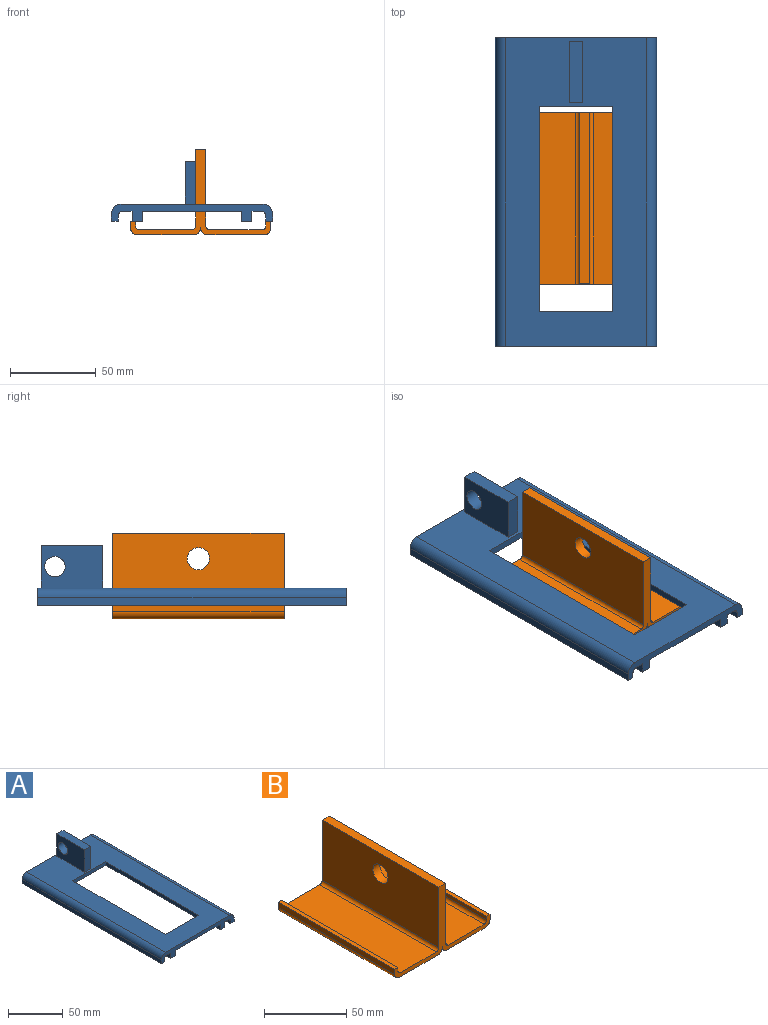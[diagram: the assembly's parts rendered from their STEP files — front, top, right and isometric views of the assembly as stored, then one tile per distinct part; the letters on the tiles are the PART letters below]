
ASSEMBLY  parts=2 mates=1
PART A: 32 faces, bbox 94x180x35 mm
  f0: plane 180x58mm, normal (0,0,-1), area 5304mm2, adj f5,f6,f20,f21,f22,f23,f24,f25
  f1: plane 180x82.8mm, normal (0,0,1), area 9480mm2, adj f14,f15,f20,f21,f22,f23,f24,f25
  f2: plane 180x5.2mm, normal (0,0,-1), area 936mm2, adj f3,f19,f20,f21
  f3: plane 180x6mm, normal (-1,0,0), area 1080mm2, adj f2,f4,f20,f21
  f4: plane 180x6mm, normal (0,0,-1), area 1080mm2, adj f3,f5,f20,f21
  f5: plane 180x6mm, normal (1,0,0), area 1080mm2, adj f0,f4,f20,f21
  f6: plane 180x6mm, normal (-1,0,0), area 1080mm2, adj f0,f7,f20,f21
  f7: plane 180x6mm, normal (0,0,-1), area 1080mm2, adj f6,f8,f20,f21
  f8: plane 180x6mm, normal (1,0,0), area 1080mm2, adj f7,f9,f20,f21
  f9: plane 180x5.2mm, normal (0,0,-1), area 936mm2, adj f8,f10,f20,f21
  f10: cylinder r=2.8mm len=180mm, axis (0,1,0), area 791.7mm2, adj f9,f11,f20,f21
  f11: plane 180x3.2mm, normal (-1,0,0), area 576mm2, adj f10,f12,f20,f21
  f12: plane 180x4mm, normal (0,0,-1), area 720mm2, adj f11,f13,f20,f21
  f13: plane 180x4.4mm, normal (1,0,0), area 792mm2, adj f12,f14,f20,f21
  f14: cylinder r=5.6mm len=180mm, axis (0,1,0), area 1583.4mm2, adj f1,f13,f20,f21
  f15: cylinder r=5.6mm len=180mm, axis (0,1,0), area 1583.4mm2, adj f1,f16,f20,f21
  f16: plane 180x4.4mm, normal (-1,0,0), area 792mm2, adj f15,f17,f20,f21
  f17: plane 180x4mm, normal (0,0,-1), area 720mm2, adj f16,f18,f20,f21
  f18: plane 180x3.2mm, normal (1,0,0), area 576mm2, adj f17,f19,f20,f21
  f19: cylinder r=2.8mm len=180mm, axis (0,1,0), area 791.7mm2, adj f2,f18,f20,f21
  f20: plane 94x10mm, normal (0,-1,0), area 485.9mm2, adj f0,f1,f2,f3,f4,f5,f6,f7
  f21: plane 94x10mm, normal (0,1,0), area 485.9mm2, adj f0,f1,f2,f3,f4,f5,f6,f7
  f22: plane 42.8x4mm, normal (0,-1,0), area 171.2mm2, adj f0,f1,f23,f25
  f23: plane 120x4mm, normal (1,0,0), area 480mm2, adj f0,f1,f22,f24
  f24: plane 42.8x4mm, normal (0,1,0), area 171.2mm2, adj f0,f1,f23,f25
  f25: plane 120x4mm, normal (-1,0,0), area 480mm2, adj f0,f1,f22,f24
  f26: plane 25x8mm, normal (0,1,0), area 200mm2, adj f1,f27,f29,f30
  f27: plane 36x25mm, normal (-1,0,0), area 786.9mm2, adj f1,f26,f28,f30,f31
  f28: plane 25x8mm, normal (0,-1,0), area 200mm2, adj f1,f27,f29,f30
  f29: plane 36x25mm, normal (1,0,0), area 786.9mm2, adj f1,f26,f28,f30,f31
  f30: plane 36x8mm, normal (0,0,1), area 288mm2, adj f26,f27,f28,f29
  f31: cylinder r=6mm len=12mm, axis (-1,0,0), area 301.6mm2, adj f27,f29
PART B: 24 faces, bbox 82x100x50 mm
  f0: cylinder r=2.1mm len=100mm, axis (0,1,0), area 329.9mm2, adj f1,f10,f11,f12
  f1: plane 100x30.8mm, normal (0,0,1), area 3080mm2, adj f0,f2,f11,f12
  f2: cylinder r=2.1mm len=100mm, axis (0,1,0), area 329.9mm2, adj f1,f3,f11,f12
  f3: plane 100x44.9mm, normal (1,0,0), area 4357.3mm2, adj f2,f4,f11,f12,f13
  f4: plane 100x6mm, normal (0,0,1), area 600mm2, adj f3,f11,f12,f17
  f5: cylinder r=4.2mm len=100mm, axis (0,1,0), area 659.7mm2, adj f6,f11,f12,f18
  f6: plane 100x32.6mm, normal (0,0,-1), area 3260mm2, adj f5,f7,f11,f12
  f7: cylinder r=4.2mm len=100mm, axis (0,1,0), area 659.7mm2, adj f6,f8,f11,f12
  f8: plane 100x3.8mm, normal (1,0,0), area 380mm2, adj f7,f9,f11,f12
  f9: plane 100x3mm, normal (0,0,1), area 300mm2, adj f8,f10,f11,f12
  f10: plane 100x2.9mm, normal (-1,0,0), area 290mm2, adj f0,f9,f11,f12
  f11: plane 82x50mm, normal (0,-1,0), area 546.6mm2, adj f0,f1,f2,f3,f4,f5,f6,f7
  f12: plane 82x50mm, normal (0,1,0), area 546.6mm2, adj f0,f1,f2,f3,f4,f5,f6,f7
  f13: cylinder r=6.5mm len=13mm, axis (1,0,0), area 245mm2, adj f3,f17
  f14: cylinder r=2.1mm len=100mm, axis (0,1,0), area 329.9mm2, adj f11,f12,f15,f23
  f15: plane 100x30.8mm, normal (0,0,1), area 3080mm2, adj f11,f12,f14,f16
  f16: cylinder r=2.1mm len=100mm, axis (0,1,0), area 329.9mm2, adj f11,f12,f15,f17
  f17: plane 100x44.9mm, normal (-1,0,0), area 4357.3mm2, adj f4,f11,f12,f13,f16
  f18: cylinder r=4.2mm len=100mm, axis (0,1,0), area 659.7mm2, adj f5,f11,f12,f19
  f19: plane 100x32.6mm, normal (0,0,-1), area 3260mm2, adj f11,f12,f18,f20
  f20: cylinder r=4.2mm len=100mm, axis (0,1,0), area 659.7mm2, adj f11,f12,f19,f21
  f21: plane 100x3.8mm, normal (-1,0,0), area 380mm2, adj f11,f12,f20,f22
  f22: plane 100x3mm, normal (0,0,1), area 300mm2, adj f11,f12,f21,f23
  f23: plane 100x2.9mm, normal (1,0,0), area 290mm2, adj f11,f12,f14,f22
PLACE A t=(-44.32,67.77,-35.81)mm
PLACE B t=(-39.25,24.04,-27.83)mm fixed
MATE parallel B.f15 <-> A.f0  axis (0,0,1) through (-59.75,-25.96,-40.72)mm
